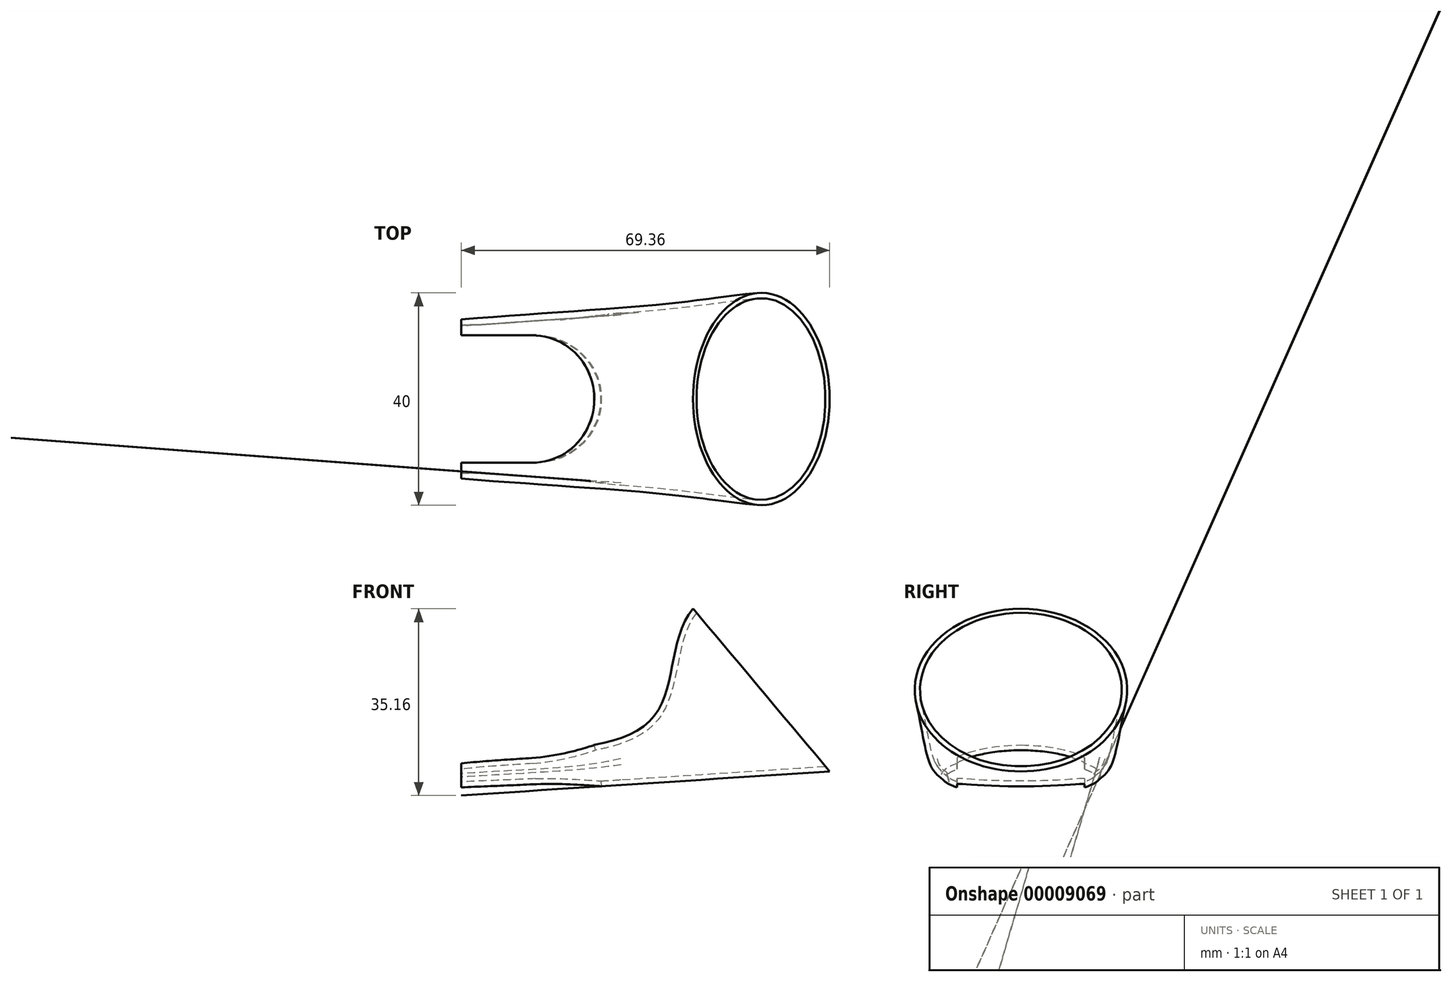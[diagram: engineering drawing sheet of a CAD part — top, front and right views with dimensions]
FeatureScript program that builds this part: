
annotation { "Feature Type Name" : "Feature", "Feature Type Description" : "" }
export const myFeature = defineFeature(function(context is Context, id is Id, definition is map)
    precondition{}
    {
        {
            var Q0;
            Q0=qCreatedBy(makeId("Top.planeOp"),FACE);
            var sketch = newSketch(context, id + "F0", { "sketchPlane" : qUnion([Q0])});
            skLineSegment(sketch, "E0", {"start": v(0, -25) * mm, "end": v(0, 25) * mm, "construction": true});
            skPoint(sketch, "E1", {"position": v(0, 0) * mm});
            skSolve(sketch);
        }
        {
            var Q0;
            Q0=qCreatedBy(makeId("Right.planeOp"),FACE);
            var Q1;
            Q1=sQuery(id+"F0.wireOp",EDGE,"E0");
            cPlane(context, id + "F1", {"entities" : qUnion([Q0, Q1]), "cplaneType" : CPlaneType.LINE_ANGLE, "offset" : 25 * mm, "angle" : 320 * degree, "width" : 150 * mm, "height" : 150 * mm});
        }
        {
            var Q0;
            Q0=qCreatedBy(id+"F1.planeOp",FACE);
            var sketch = newSketch(context, id + "F2", { "sketchPlane" : qUnion([Q0])});
            skCircle(sketch, "E2", {"center": v(0, 21) * mm, "radius": 20 * mm});
            skPoint(sketch, "E3", {"position": v(20, 21) * mm});
            skPoint(sketch, "E4", {"position": v(-20, 21) * mm});
            skSolve(sketch);
        }
        {
            var Q0;
            Q0=qCreatedBy(makeId("Right.planeOp"),FACE);
            cPlane(context, id + "F3", {"entities" : qUnion([Q0]), "cplaneType" : CPlaneType.OFFSET, "offset" : 70 * mm, "oppositeDirection" : true, "width" : 150 * mm, "height" : 150 * mm});
        }
        {
            var Q0;
            Q0=qCreatedBy(id+"F3.planeOp",FACE);
            var sketch = newSketch(context, id + "F4", { "sketchPlane" : qUnion([Q0])});
            skEllipse(sketch, "E5", {"center": v(0, 0) * mm, "majorRadius": 15 * mm, "minorRadius": 3.75 * mm, "majorAxis": v(-1, 0)});
            skPoint(sketch, "E6", {"position": v(15, 0) * mm});
            skPoint(sketch, "E7", {"position": v(-15, 0) * mm});
            skLineSegment(sketch, "E8", {"start": v(15, 0) * mm, "end": v(-15, 0) * mm, "construction": true});
            skSolve(sketch);
        }
        {
            var Q0;
            Q0=qCreatedBy(makeId("Front.planeOp"),FACE);
            var sketch = newSketch(context, id + "F5", { "sketchPlane" : qUnion([Q0])});
            skFitSpline(sketch, "E9", {"points": [v(-26.35, 31.4) * mm, v(-34.6, 10.19) * mm, v(-70, 3.75) * mm], "startDerivative": vector(-33.13, -39.08) * mm, "endDerivative": vector(-55.43, -5.93) * mm});
            skLineSegment(sketch, "E10", {"start": v(-70, -3.75) * mm, "end": v(-0.64, 0.77) * mm});
            skSolve(sketch);
        }
        {
            var Q0;
            Q0=makeQuery(id+"F2.imprint","IMPRINT",FACE,{"disambiguationData":[TD([[makeQuery(id+"F2.imprint","IMPRINT",EDGE,{"derivedFrom":sQuery(id+"F2.wireOp",EDGE,"E2")}),1.0]])]});
            var Q1;
            Q1=makeQuery(id+"F4.imprint","IMPRINT",FACE,{"disambiguationData":[TD([[makeQuery(id+"F4.imprint","IMPRINT",EDGE,{"derivedFrom":sQuery(id+"F4.wireOp",EDGE,"E5")}),1.0]])]});
            var Q2;
            Q2=sQuery(id+"F5.wireOp",EDGE,"E9");
            var Q3;
            Q3=sQuery(id+"F5.wireOp",EDGE,"E10");
            var Q4;
            Q4=sQuery(id+"F2.wireOp",VERTEX,"E3");
            var Q5;
            Q5=sQuery(id+"F4.wireOp",VERTEX,"E7");
            loft(context, id + "F6", {"addGuides" : true, "sheetProfilesArray" : [{ "sheetProfileEntities" : qUnion([Q0]) }, { "sheetProfileEntities" : qUnion([Q1]) }], "guidesArray" : [{ "guideEntities" : qUnion([Q2]), "guideDerivativeType" : LoftGuideDerivativeType.DEFAULT, "guideDerivativeMagnitude" : 1 }, { "guideEntities" : qUnion([Q3]), "guideDerivativeType" : LoftGuideDerivativeType.DEFAULT, "guideDerivativeMagnitude" : 1 }], "connections" : [{ "connectionEntities" : qUnion([Q4, Q5]), "connectionEdgeQueries" : qUnion([]), "connectionEdgeParameters" : [] }]});
        }
        {
            var Q0;
            Q0=makeQuery(id+"F6.opLoft","CAP_FACE",FACE,{"disambiguationData":[OSD([makeQuery(id+"F2.imprint","IMPRINT",FACE,{"disambiguationData":[TD([[makeQuery(id+"F2.imprint","IMPRINT",EDGE,{"derivedFrom":sQuery(id+"F2.wireOp",EDGE,"E2")}),1.0]])]})])],"isStart":true});
            var Q1;
            Q1=makeQuery(id+"F6.opLoft","CAP_FACE",FACE,{"disambiguationData":[OSD([makeQuery(id+"F4.imprint","IMPRINT",FACE,{"disambiguationData":[TD([[makeQuery(id+"F4.imprint","IMPRINT",EDGE,{"derivedFrom":sQuery(id+"F4.wireOp",EDGE,"E5")}),1.0]])]})])],"isStart":true});
            shell(context, id + "F7", {"entities" : qUnion([Q0, Q1]), "thickness" : 1 * mm});
        }
        {
            var Q0;
            Q0=qCreatedBy(makeId("Top.planeOp"),FACE);
            var Q1;
            Q1=sQuery(id+"F4.wireOp",EDGE,"E8");
            cPlane(context, id + "F8", {"entities" : qUnion([Q0, Q1]), "cplaneType" : CPlaneType.LINE_ANGLE, "offset" : 25 * mm, "angle" : 10 * degree, "width" : 150 * mm, "height" : 150 * mm});
        }
        {
            var Q0;
            Q0=qCreatedBy(id+"F8.planeOp",FACE);
            var sketch = newSketch(context, id + "F9", { "sketchPlane" : qUnion([Q0])});
            skCircle(sketch, "E11", {"center": v(-55.29, 0) * mm, "radius": 12 * mm});
            skLineSegment(sketch, "E12", {"start": v(-55.29, -12) * mm, "end": v(-77.29, -12) * mm});
            skLineSegment(sketch, "E13", {"start": v(-77.29, -12) * mm, "end": v(-77.29, 12) * mm});
            skLineSegment(sketch, "E14", {"start": v(-77.29, 12) * mm, "end": v(-55.29, 12) * mm});
            skSolve(sketch);
        }
        {
            var Q0;
            Q0=makeQuery(id+"F9.imprint","IMPRINT",FACE,{"disambiguationData":[TD([[makeQuery(id+"F9.imprint","IMPRINT",EDGE,{"derivedFrom":sQuery(id+"F9.wireOp",EDGE,"E11")}),1.0]])]});
            var Q1;
            {var subQ0=sQuery(id+"F9.wireOp",EDGE,"E12");Q1=makeQuery(id+"F9.imprint","IMPRINT",FACE,{"disambiguationData":[TD([[makeQuery(id+"F9.imprint","IMPRINT",EDGE,{"derivedFrom":subQ0}),-1.0]])]});}
            extrude(context, id + "F10", {"entities" : qUnion([Q0, Q1]), "operationType" : NewBodyOperationType.REMOVE, "oppositeDirection" : true, "depth" : 25 * mm, "hasSecondDirection" : true, "secondDirectionOppositeDirection" : false, "secondDirectionDepth" : 25 * mm});
        }
    });
